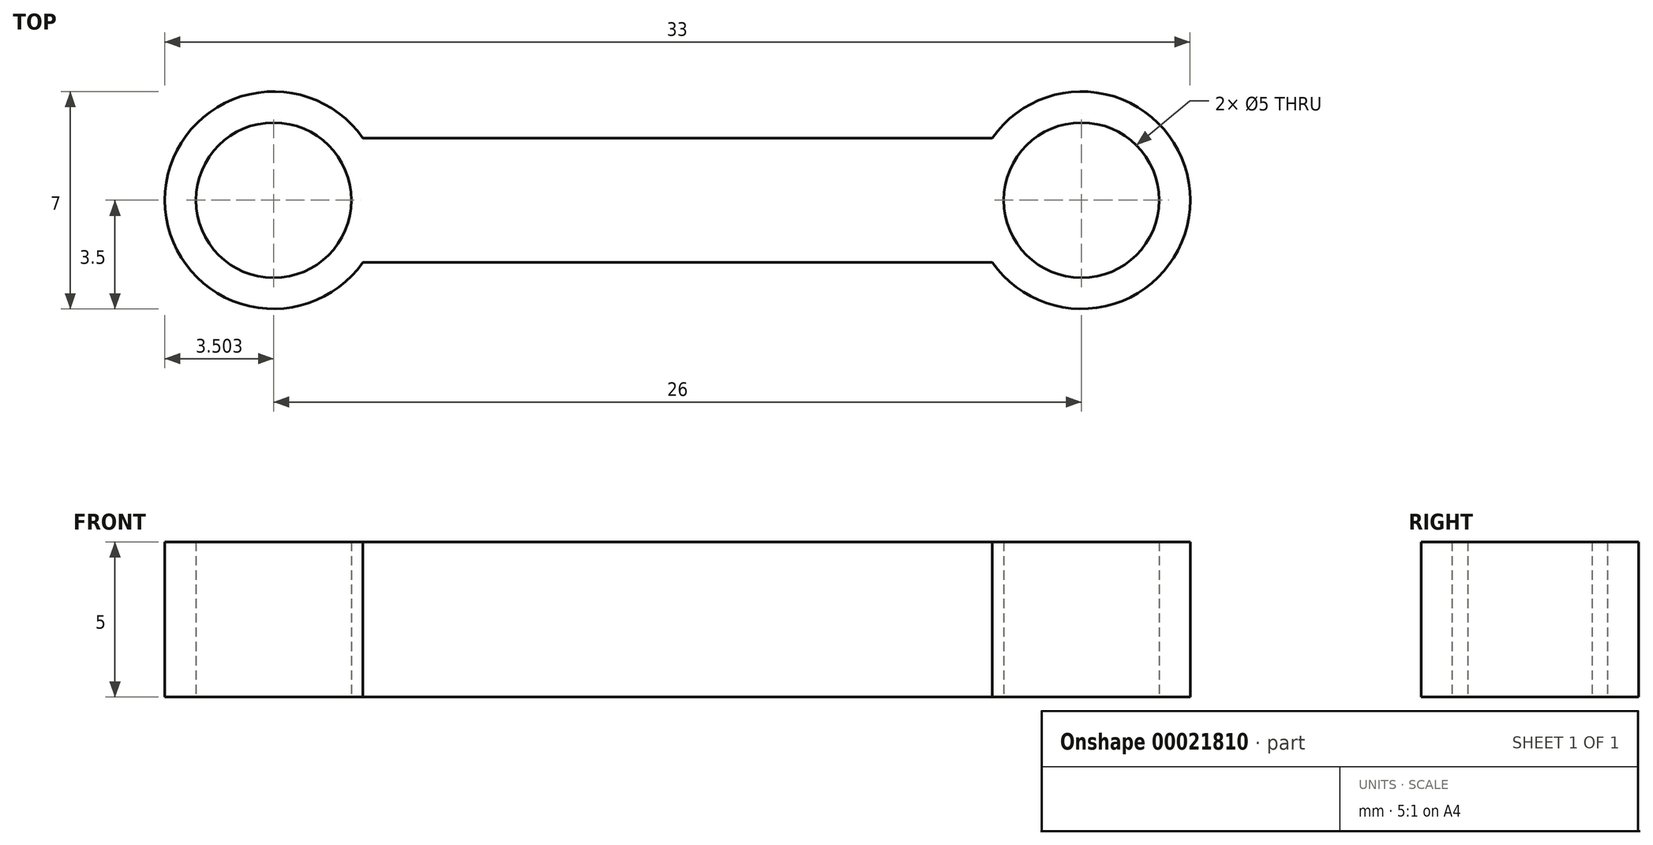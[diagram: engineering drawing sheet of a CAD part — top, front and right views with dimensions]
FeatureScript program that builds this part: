
annotation { "Feature Type Name" : "Feature", "Feature Type Description" : "" }
export const myFeature = defineFeature(function(context is Context, id is Id, definition is map)
    precondition{}
    {
        {
            var Q0;
            Q0=qCreatedBy(makeId("Top.planeOp"),FACE);
            var sketch = newSketch(context, id + "F0", { "sketchPlane" : qUnion([Q0])});
            skCircle(sketch, "E0", {"center": v(-4.76, 0) * mm, "radius": 2.5 * mm});
            skCircle(sketch, "E1", {"center": v(21.24, 0) * mm, "radius": 2.5 * mm});
            skLineSegment(sketch, "E2", {"start": v(-3.26, 2) * mm, "end": v(19.74, 2) * mm});
            skPoint(sketch, "E3.start.orphan", {"position": v(-0.94, 0) * mm});
            skCircle(sketch, "E4", {"center": v(21.24, 0) * mm, "radius": 3.5 * mm});
            skCircle(sketch, "E5", {"center": v(-4.76, 0) * mm, "radius": 3.5 * mm});
            skLineSegment(sketch, "E6.MirrorCS", {"start": v(-3.26, -2) * mm, "end": v(19.74, -2) * mm});
            skSolve(sketch);
        }
        {
            var Q0;
            {var subQ3=sQuery(id+"F0.wireOp",EDGE,"E2");var subQ5=sQuery(id+"F0.wireOp",EDGE,"E0");var subQ6=makeQuery(id+"F0.imprint","INTERSECT",VERTEX,{"derivedFrom":[subQ5,subQ3]});Q0=makeQuery(id+"F0.imprint","IMPRINT",FACE,{"disambiguationData":[TD([[makeQuery(id+"F0.imprint","IMPRINT",EDGE,{"disambiguationData":[TD([[subQ6,-1.0]])],"derivedFrom":subQ5}),-1.0]])]});}
            var Q1;
            {var subQ3=sQuery(id+"F0.wireOp",EDGE,"E2");var subQ5=sQuery(id+"F0.wireOp",EDGE,"E1");var subQ7=makeQuery(id+"F0.imprint","INTERSECT",VERTEX,{"derivedFrom":[subQ5,subQ3]});Q1=makeQuery(id+"F0.imprint","IMPRINT",FACE,{"disambiguationData":[TD([[makeQuery(id+"F0.imprint","IMPRINT",EDGE,{"disambiguationData":[TD([[subQ7,-1.0]])],"derivedFrom":subQ5}),-1.0]])]});}
            var Q2;
            {var subQ0=sQuery(id+"F0.wireOp",EDGE,"E5");var subQ3=sQuery(id+"F0.wireOp",EDGE,"E2");var subQ4=makeQuery(id+"F0.imprint","INTERSECT",VERTEX,{"derivedFrom":[subQ3,subQ0]});Q2=makeQuery(id+"F0.imprint","IMPRINT",FACE,{"disambiguationData":[TD([[makeQuery(id+"F0.imprint","IMPRINT",EDGE,{"disambiguationData":[TD([[subQ4,-1.0]])],"derivedFrom":subQ3}),-1.0]])]});}
            var Q3;
            {var subQ3=sQuery(id+"F0.wireOp",EDGE,"E2");var subQ5=sQuery(id+"F0.wireOp",EDGE,"E0");var subQ7=makeQuery(id+"F0.imprint","INTERSECT",VERTEX,{"derivedFrom":[subQ5,subQ3]});Q3=makeQuery(id+"F0.imprint","IMPRINT",FACE,{"disambiguationData":[TD([[makeQuery(id+"F0.imprint","IMPRINT",EDGE,{"disambiguationData":[TD([[subQ7,1.0]])],"derivedFrom":subQ5}),-1.0]])]});}
            var Q4;
            {var subQ3=sQuery(id+"F0.wireOp",EDGE,"E2");var subQ5=sQuery(id+"F0.wireOp",EDGE,"E1");var subQ7=makeQuery(id+"F0.imprint","INTERSECT",VERTEX,{"derivedFrom":[subQ5,subQ3]});Q4=makeQuery(id+"F0.imprint","IMPRINT",FACE,{"disambiguationData":[TD([[makeQuery(id+"F0.imprint","IMPRINT",EDGE,{"disambiguationData":[TD([[subQ7,1.0]])],"derivedFrom":subQ5}),-1.0]])]});}
            extrude(context, id + "F1", {"entities" : qUnion([Q0, Q1, Q2, Q3, Q4]), "depth" : 5 * mm});
        }
    });
